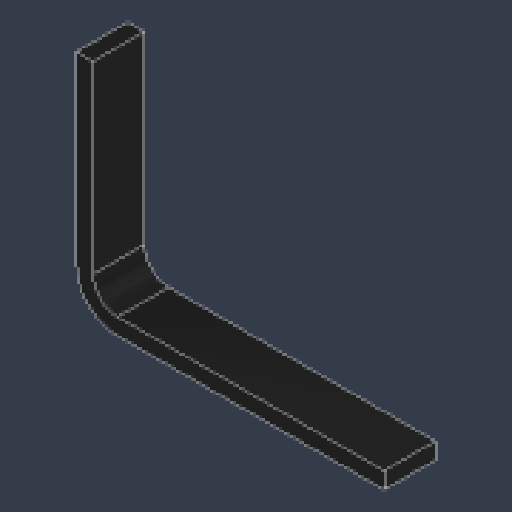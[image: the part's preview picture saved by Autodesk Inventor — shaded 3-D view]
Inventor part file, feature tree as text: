
AUTODESK INVENTOR PART (.ipt)
format: ipt  version: 2023.4 (Build 274418000, 418)  size: 145,408 bytes
history: native  units: mm
features: fillet x4, sketch x3, extrude x2, hole x1
ambient origin geometry x8: Origin, YZ Plane, XZ Plane, XY Plane, X Axis, Y Axis, Z Axis, Center Point
bodies: Solid1 (feature_tree)
feature tree (10):
  extrude  "Extrusion1"  Depth=109.6mm
  fillet  "Fillet1"  Radius=8.0mm
  fillet  "Fillet2"  Radius=8.0mm
  extrude  "Extrusion2"  Depth=25.0mm
  hole  "Hole1"  [1 undecoded]
  fillet  "Fillet3"  Radius=10.0mm
  fillet  "Fillet4"  Radius=14.0mm
  sketch  "Sketch1"  dims[d0=149.6mm d1=109.6mm d2=8.0mm d3=8.0mm]
  sketch  "Sketch2"  dims[d4=25.0mm d5=0.0mm d6=12.0mm]
  sketch  "Sketch3"  dims[d7=20.0mm d8=10.0mm d9=10.0mm d10=14.0mm d11=14.0mm d12=73.0mm d13=100.0mm d14=10.0mm d15=25.0mm d16=0.0mm d17=5.6mm d18=6.0mm d19=7.5mm d20=2.0mm d21=90.0deg d22=15.0mm d23=0.0mm d24=5.0mm d25=0.4mm]
note: 1 required parameter value undecoded (feature->parameter linkage not recoverable at this tier; creation-order binding heuristic only, values carry confidence <= 0.55)
